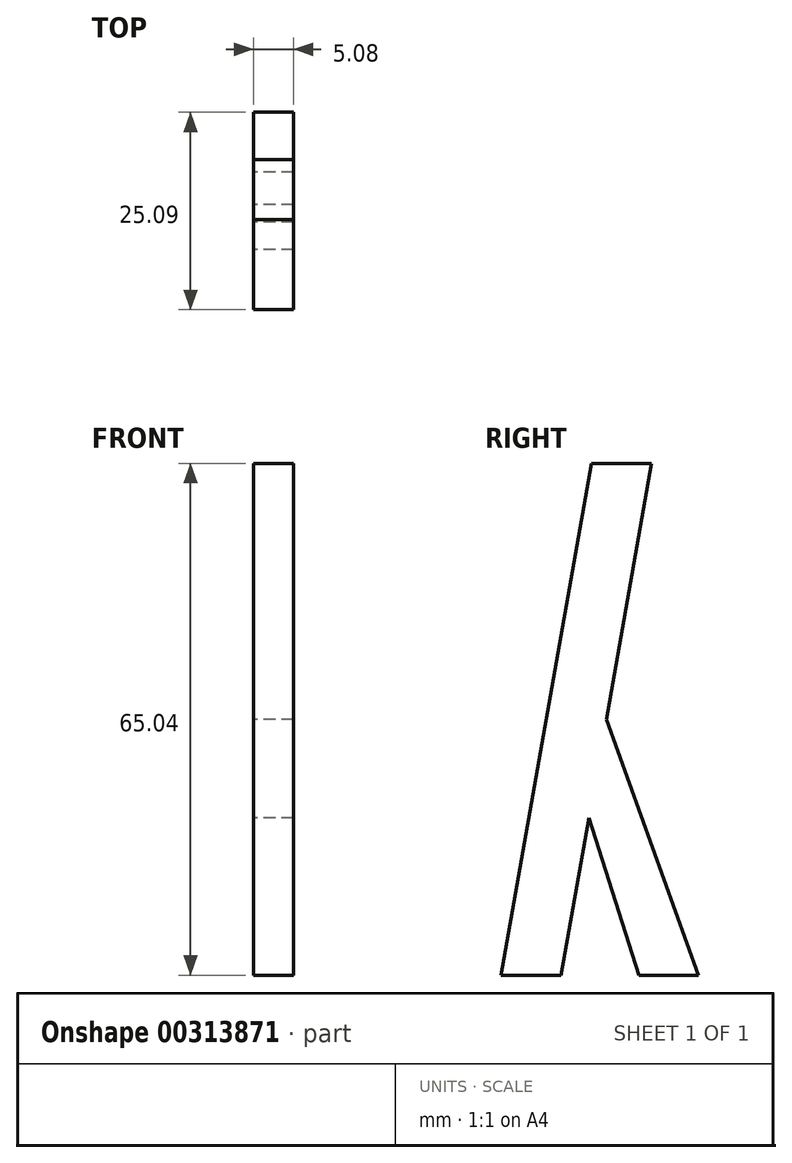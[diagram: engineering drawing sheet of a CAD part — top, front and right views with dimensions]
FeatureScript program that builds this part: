
annotation { "Feature Type Name" : "Feature", "Feature Type Description" : "" }
export const myFeature = defineFeature(function(context is Context, id is Id, definition is map)
    precondition{}
    {
        {
            var Q0;
            Q0=qCreatedBy(makeId("Right.planeOp"),FACE);
            var sketch = newSketch(context, id + "F0", { "sketchPlane" : qUnion([Q0])});
            skLineSegment(sketch, "E0.top", {"start": v(1.62, 65.04) * mm, "end": v(-6, 65.04) * mm});
            skLineSegment(sketch, "E0.right", {"start": v(-17.47, 0) * mm, "end": v(-6, 65.04) * mm});
            skLineSegment(sketch, "E1", {"start": v(1.62, 65.04) * mm, "end": v(-9.85, 0) * mm});
            skLineSegment(sketch, "E2", {"start": v(-17.47, 0) * mm, "end": v(-9.85, 0) * mm});
            skLineSegment(sketch, "E3", {"start": v(-6.32, 20.01) * mm, "end": v(0, 0) * mm});
            skLineSegment(sketch, "E4", {"start": v(0, 0) * mm, "end": v(7.62, 0) * mm});
            skLineSegment(sketch, "E5", {"start": v(7.62, 0) * mm, "end": v(-4.11, 32.52) * mm});
            skSolve(sketch);
        }
        {
            var Q0;
            {var subQ3=sQuery(id+"F0.wireOp",EDGE,"E0.top");Q0=makeQuery(id+"F0.imprint","IMPRINT",FACE,{"disambiguationData":[TD([[makeQuery(id+"F0.imprint","IMPRINT",EDGE,{"derivedFrom":subQ3}),1.0]])]});}
            var Q1;
            {var subQ0=sQuery(id+"F0.wireOp",EDGE,"E3");Q1=makeQuery(id+"F0.imprint","IMPRINT",FACE,{"disambiguationData":[TD([[makeQuery(id+"F0.imprint","IMPRINT",EDGE,{"derivedFrom":subQ0}),1.0]])]});}
            extrude(context, id + "F1", {"entities" : qUnion([Q0, Q1]), "depth" : 5.08 * mm});
        }
    });
